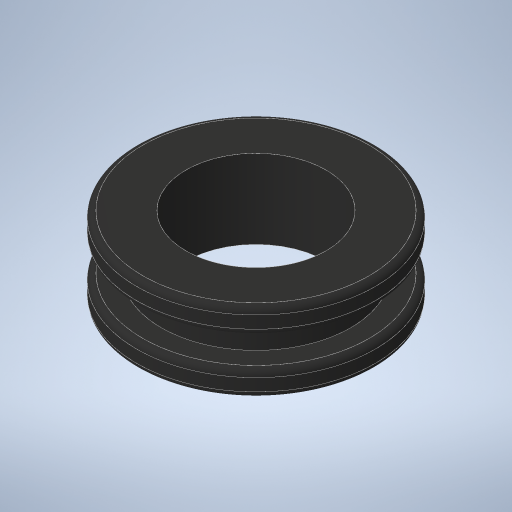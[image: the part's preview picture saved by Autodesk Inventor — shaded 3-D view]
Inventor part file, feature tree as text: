
AUTODESK INVENTOR PART (.ipt)
format: ipt  version: 2023.4 (Build 274418000, 418)  size: 277,504 bytes
history: native  units: in
note: dims shown in document units (in); Inventor stores cm internally (conversion verified against a paired STEP export)
features: revolve x1, fillet x1, chamfer x1, sketch x1
ambient origin geometry x8: Origin, YZ Plane, XZ Plane, XY Plane, X Axis, Y Axis, Z Axis, Center Point
bodies: Solid1 (feature_tree)
feature tree (4):
  revolve  "Revolution1"  [1 undecoded]
  fillet  "Fillet1"  Radius=0.2in
  chamfer  "Chamfer1"  Distance=0.0625in
  sketch  "Sketch1"  dims[d0=0.24in d1=0.075in d2=0.2in d3=0.0625in d4=0.0625in d5=0.0625in d6=90.0deg d7=0.0156in d8=0.0312in d9=0.125in d10=45.0deg]
note: 1 required parameter value undecoded (feature->parameter linkage not recoverable at this tier; creation-order binding heuristic only, values carry confidence <= 0.55)
